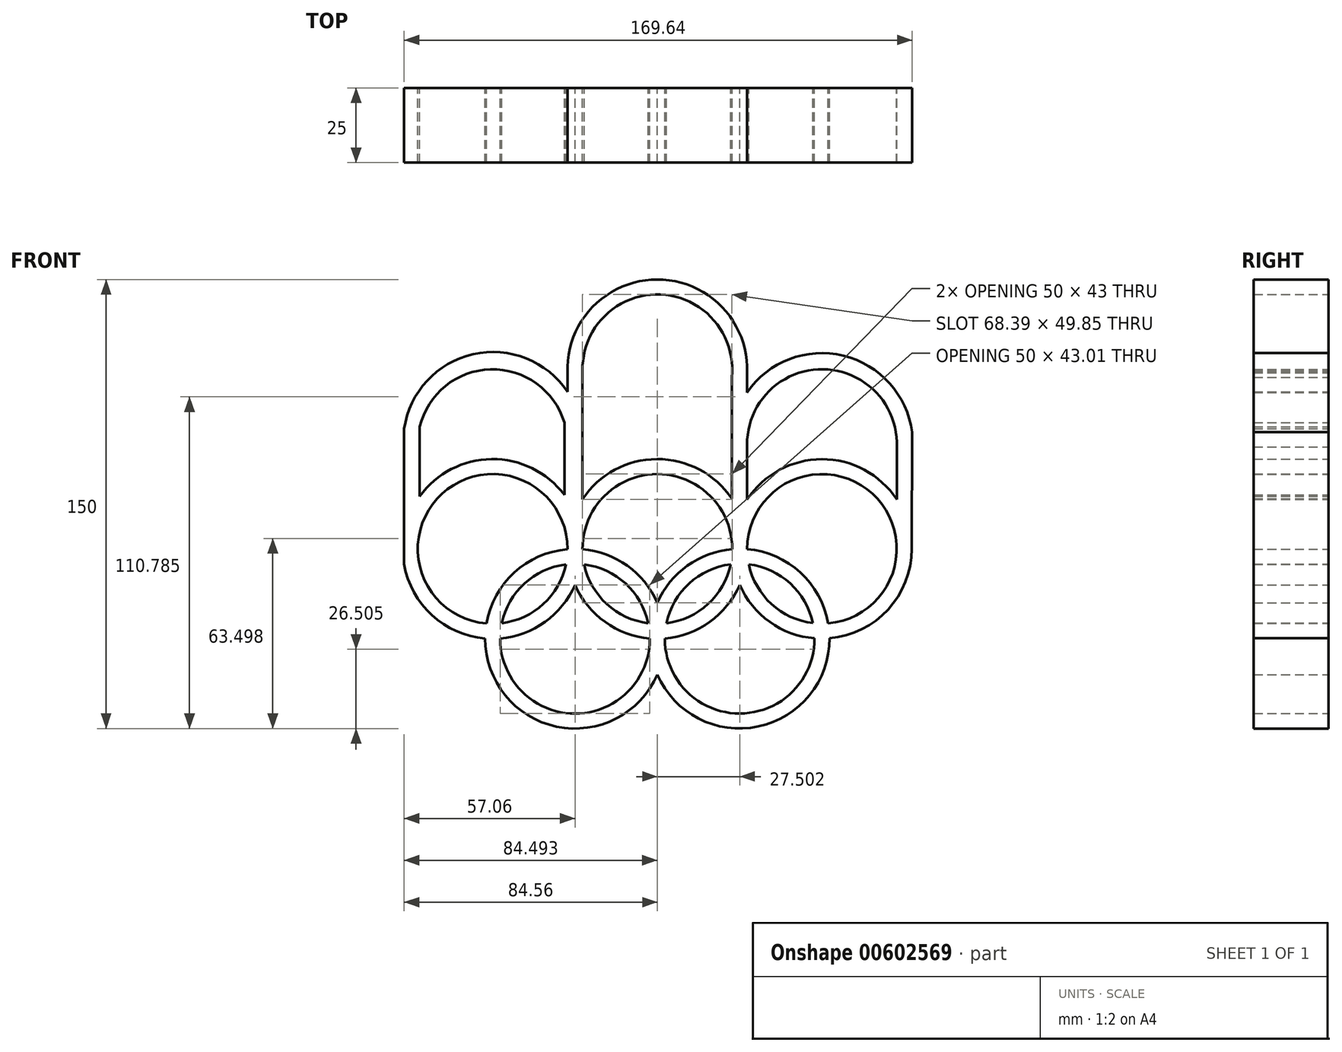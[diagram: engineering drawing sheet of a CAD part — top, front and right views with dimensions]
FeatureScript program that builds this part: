
annotation { "Feature Type Name" : "Feature", "Feature Type Description" : "" }
export const myFeature = defineFeature(function(context is Context, id is Id, definition is map)
    precondition{}
    {
        {
            var Q0;
            Q0=qCreatedBy(makeId("Front.planeOp"),FACE);
            var sketch = newSketch(context, id + "F0", { "sketchPlane" : qUnion([Q0])});
            skArc(sketch, "E0", {"start": v(-24.46, -5.19) * mm, "mid": v(-16.9, -18.43) * mm, "end": v(-3.04, -24.81) * mm});
            skArc(sketch, "E1", {"start": v(-27.5, -11.99) * mm, "mid": v(-17.47, -24.39) * mm, "end": v(-2.5, -29.9) * mm});
            skArc(sketch, "E2", {"start": v(-31.05, 18.06) * mm, "mid": v(-55.31, 30) * mm, "end": v(-79.32, 17.56) * mm});
            skArc(sketch, "E3", {"start": v(-30, -0.1) * mm, "mid": v(-71.9, 18.43) * mm, "end": v(-57.07, -24.91) * mm});
            skArc(sketch, "E4", {"start": v(27.5, -11.99) * mm, "mid": v(37.53, -24.37) * mm, "end": v(52.5, -29.86) * mm});
            skArc(sketch, "E5", {"start": v(30.54, -5.17) * mm, "mid": v(38.1, -18.4) * mm, "end": v(51.95, -24.78) * mm});
            skArc(sketch, "E6.trimOffspring", {"start": v(24.86, 16.8) * mm, "mid": v(-0.12, 30) * mm, "end": v(-25, 16.6) * mm});
            skLineSegment(sketch, "E7", {"start": v(-84.56, 40.11) * mm, "end": v(-84.56, -5.11) * mm});
            skLineSegment(sketch, "E8", {"start": v(-31.05, 42.16) * mm, "end": v(-31.05, 18.06) * mm});
            skLineSegment(sketch, "E9", {"start": v(-79.32, 40.78) * mm, "end": v(-79.32, 17.56) * mm});
            skArc(sketch, "E10.trimOffspring", {"start": v(-31.05, 42.16) * mm, "mid": v(-55.72, 59.99) * mm, "end": v(-79.32, 40.78) * mm});
            skArc(sketch, "E11.trimOffspring", {"start": v(-84.56, -5.11) * mm, "mid": v(-75.26, -22.12) * mm, "end": v(-57.5, -29.9) * mm});
            skArc(sketch, "E12", {"start": v(24.86, 57.35) * mm, "mid": v(1.05, 84.98) * mm, "end": v(-25, 59.44) * mm});
            skLineSegment(sketch, "E13", {"start": v(-25, 59.44) * mm, "end": v(-25, 16.6) * mm});
            skLineSegment(sketch, "E14", {"start": v(-29.98, 58.84) * mm, "end": v(-29.98, 52.48) * mm});
            skArc(sketch, "E15.trimOffspring", {"start": v(-29.98, 52.48) * mm, "mid": v(-61.5, 65) * mm, "end": v(-84.56, 40.11) * mm});
            skLineSegment(sketch, "E16", {"start": v(85.08, 38.97) * mm, "end": v(84.93, 0) * mm});
            skLineSegment(sketch, "E17", {"start": v(29.98, 58.9) * mm, "end": v(29.98, 52.28) * mm});
            skLineSegment(sketch, "E18", {"start": v(29.97, 35.24) * mm, "end": v(29.97, 16.52) * mm});
            skLineSegment(sketch, "E19", {"start": v(24.86, 57.35) * mm, "end": v(24.86, 16.8) * mm});
            skArc(sketch, "E20.trimOffspring", {"start": v(29.98, 58.9) * mm, "mid": v(-0.03, 90) * mm, "end": v(-29.98, 58.84) * mm});
            skLineSegment(sketch, "E21", {"start": v(79.95, 35.96) * mm, "end": v(79.95, 16.55) * mm});
            skArc(sketch, "E22.trimOffspring", {"start": v(79.95, 34.04) * mm, "mid": v(55.33, 60) * mm, "end": v(29.97, 34.76) * mm});
            skArc(sketch, "E23.trimOffspring", {"start": v(85.08, 38.97) * mm, "mid": v(62.1, 64.53) * mm, "end": v(29.98, 52.28) * mm});
            skArc(sketch, "E24", {"start": v(-30, -0.1) * mm, "mid": v(-47.77, -7.89) * mm, "end": v(-57.07, -24.91) * mm});
            skArc(sketch, "E25", {"start": v(-30.54, -5.19) * mm, "mid": v(-44.4, -11.57) * mm, "end": v(-51.96, -24.81) * mm});
            skArc(sketch, "E26", {"start": v(25, -0.09) * mm, "mid": v(10.03, -5.6) * mm, "end": v(0, -18) * mm});
            skArc(sketch, "E27", {"start": v(24.46, -5.17) * mm, "mid": v(10.6, -11.56) * mm, "end": v(3.04, -24.81) * mm});
            skArc(sketch, "E28.trimOffspring", {"start": v(-52.5, -29.9) * mm, "mid": v(-27.5, -55) * mm, "end": v(-2.5, -29.9) * mm});
            skArc(sketch, "E29.trimOffspring", {"start": v(-51.96, -24.81) * mm, "mid": v(-38.1, -18.43) * mm, "end": v(-30.54, -5.19) * mm});
            skArc(sketch, "E30.trimOffspring", {"start": v(-57.5, -29.9) * mm, "mid": v(-33.67, -59.36) * mm, "end": v(0, -41.98) * mm});
            skArc(sketch, "E31.trimOffspring", {"start": v(-52.5, -29.9) * mm, "mid": v(-37.53, -24.39) * mm, "end": v(-27.5, -11.99) * mm});
            skArc(sketch, "E32.trimOffspring", {"start": v(25, -0.09) * mm, "mid": v(0, 25) * mm, "end": v(-25, -0.1) * mm});
            skArc(sketch, "E33.trimOffspring", {"start": v(51.95, -24.78) * mm, "mid": v(44.39, -11.55) * mm, "end": v(30.54, -5.17) * mm});
            skArc(sketch, "E34.trimOffspring", {"start": v(57.06, -24.88) * mm, "mid": v(71.83, 18.4) * mm, "end": v(30, -0.09) * mm});
            skArc(sketch, "E35.trimOffspring", {"start": v(57.06, -24.88) * mm, "mid": v(47.77, -7.86) * mm, "end": v(30, -0.09) * mm});
            skArc(sketch, "E36.trimOffspring", {"start": v(57.5, -29.86) * mm, "mid": v(77.03, -20.27) * mm, "end": v(84.93, 0) * mm});
            skArc(sketch, "E37.trimOffspring", {"start": v(0, -18) * mm, "mid": v(-10.03, -5.6) * mm, "end": v(-25, -0.1) * mm});
            skArc(sketch, "E38.trimOffspring", {"start": v(0, -41.98) * mm, "mid": v(33.7, -59.34) * mm, "end": v(57.5, -29.86) * mm});
            skArc(sketch, "E39.trimOffspring", {"start": v(2.5, -29.9) * mm, "mid": v(27.52, -54.98) * mm, "end": v(52.5, -29.86) * mm});
            skArc(sketch, "E40.trimOffspring", {"start": v(-3.04, -24.81) * mm, "mid": v(-10.6, -11.57) * mm, "end": v(-24.46, -5.19) * mm});
            skArc(sketch, "E41.trimOffspring", {"start": v(3.04, -24.81) * mm, "mid": v(16.9, -18.42) * mm, "end": v(24.46, -5.17) * mm});
            skArc(sketch, "E42.trimOffspring", {"start": v(2.5, -29.9) * mm, "mid": v(17.47, -24.39) * mm, "end": v(27.5, -11.99) * mm});
            skArc(sketch, "E43.trimOffspring", {"start": v(79.95, 16.55) * mm, "mid": v(54.95, 29.96) * mm, "end": v(29.97, 16.52) * mm});
            skSolve(sketch);
        }
        {
            var Q0;
            Q0 = qSketchRegion(id + "F0", true);
            extrude(context, id + "F1", {"entities" : qUnion([Q0]), "depth" : 25 * mm, "offsetDistance" : 25 * mm});
        }
    });
